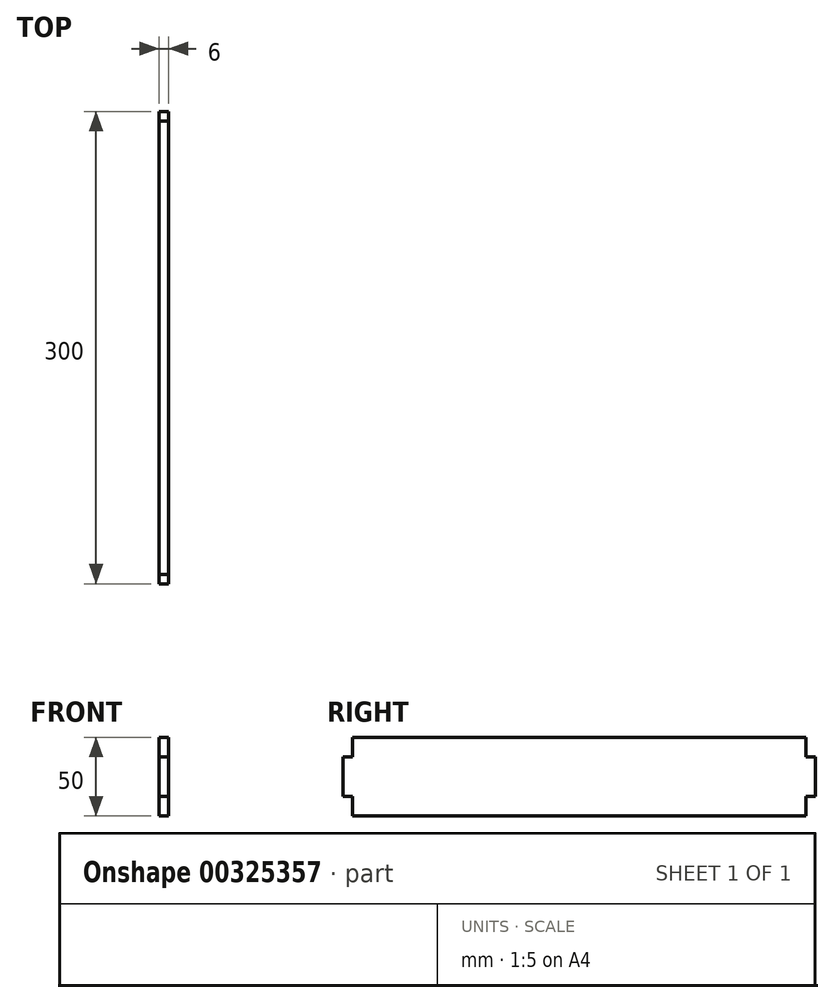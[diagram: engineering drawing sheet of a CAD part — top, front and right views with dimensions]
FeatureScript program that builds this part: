
annotation { "Feature Type Name" : "Feature", "Feature Type Description" : "" }
export const myFeature = defineFeature(function(context is Context, id is Id, definition is map)
    precondition{}
    {
        {
            var Q0;
            Q0=qCreatedBy(makeId("Right.planeOp"),FACE);
            var sketch = newSketch(context, id + "F0", { "sketchPlane" : qUnion([Q0])});
            skLineSegment(sketch, "E0.bottom", {"start": v(-144, 25) * mm, "end": v(144, 25) * mm});
            skLineSegment(sketch, "E0.top", {"start": v(-144, -25) * mm, "end": v(144, -25) * mm});
            skLineSegment(sketch, "E0.left", {"start": v(-144, 25) * mm, "end": v(-144, -25) * mm});
            skLineSegment(sketch, "E0.right", {"start": v(144, 25) * mm, "end": v(144, -25) * mm});
            skPoint(sketch, "E0.middle", {"position": v(0, 0) * mm});
            skLineSegment(sketch, "E1.bottom", {"start": v(-75, 25) * mm, "end": v(75, 25) * mm});
            skLineSegment(sketch, "E1.top", {"start": v(-75, 19) * mm, "end": v(75, 19) * mm});
            skLineSegment(sketch, "E1.left", {"start": v(-75, 25) * mm, "end": v(-75, 19) * mm});
            skLineSegment(sketch, "E1.right", {"start": v(75, 25) * mm, "end": v(75, 19) * mm});
            skPoint(sketch, "E1.middle", {"position": v(0, 22) * mm});
            skLineSegment(sketch, "E2.bottom", {"start": v(-144, 12.5) * mm, "end": v(-138, 12.5) * mm});
            skLineSegment(sketch, "E2.top", {"start": v(-144, -12.5) * mm, "end": v(-138, -12.5) * mm});
            skLineSegment(sketch, "E2.left", {"start": v(-144, 12.5) * mm, "end": v(-144, -12.5) * mm});
            skLineSegment(sketch, "E2.right", {"start": v(-138, 12.5) * mm, "end": v(-138, -12.5) * mm});
            skPoint(sketch, "E2.middle", {"position": v(-141, 0) * mm});
            skLineSegment(sketch, "E3.bottom", {"start": v(144, 12.5) * mm, "end": v(138, 12.5) * mm});
            skLineSegment(sketch, "E3.top", {"start": v(144, -12.5) * mm, "end": v(138, -12.5) * mm});
            skLineSegment(sketch, "E3.left", {"start": v(144, 12.5) * mm, "end": v(144, -12.5) * mm});
            skLineSegment(sketch, "E3.right", {"start": v(138, 12.5) * mm, "end": v(138, -12.5) * mm});
            skPoint(sketch, "E3.middle", {"position": v(141, 0) * mm});
            skPoint(sketch, "E3.middle.positionSnap0", {"position": v(144, 0) * mm});
            skPoint(sketch, "E3.centerSnap0", {"position": v(144, 0) * mm});
            skLineSegment(sketch, "E4.bottom", {"start": v(-75, -25) * mm, "end": v(75, -25) * mm});
            skLineSegment(sketch, "E4.top", {"start": v(-75, -19) * mm, "end": v(75, -19) * mm});
            skLineSegment(sketch, "E4.left", {"start": v(-75, -25) * mm, "end": v(-75, -19) * mm});
            skLineSegment(sketch, "E4.right", {"start": v(75, -25) * mm, "end": v(75, -19) * mm});
            skPoint(sketch, "E4.middle", {"position": v(0, -22) * mm});
            skLineSegment(sketch, "E5.top", {"start": v(-75, 31) * mm, "end": v(75, 31) * mm});
            skLineSegment(sketch, "E5.left", {"start": v(-75, 25) * mm, "end": v(-75, 31) * mm});
            skLineSegment(sketch, "E5.right", {"start": v(75, 25) * mm, "end": v(75, 31) * mm});
            skLineSegment(sketch, "E6.top", {"start": v(-75, -31) * mm, "end": v(75, -31) * mm});
            skLineSegment(sketch, "E6.left", {"start": v(-75, -25) * mm, "end": v(-75, -31) * mm});
            skLineSegment(sketch, "E6.right", {"start": v(75, -25) * mm, "end": v(75, -31) * mm});
            skLineSegment(sketch, "E7.bottom", {"start": v(-144, 12.5) * mm, "end": v(-150, 12.5) * mm});
            skLineSegment(sketch, "E7.top", {"start": v(-144, -12.5) * mm, "end": v(-150, -12.5) * mm});
            skLineSegment(sketch, "E7.right", {"start": v(-150, 12.5) * mm, "end": v(-150, -12.5) * mm});
            skLineSegment(sketch, "E8.bottom", {"start": v(144, 12.5) * mm, "end": v(150, 12.5) * mm});
            skLineSegment(sketch, "E8.top", {"start": v(144, -12.5) * mm, "end": v(150, -12.5) * mm});
            skLineSegment(sketch, "E8.right", {"start": v(150, 12.5) * mm, "end": v(150, -12.5) * mm});
            skSolve(sketch);
        }
        {
            var Q0;
            Q0=makeQuery(id+"F0.imprint","IMPRINT",FACE,{"disambiguationData":[TD([[makeQuery(id+"F0.imprint","IMPRINT",EDGE,{"derivedFrom":sQuery(id+"F0.wireOp",EDGE,"E1.top")}),-1.0]])]});
            var Q1;
            Q1=makeQuery(id+"F0.imprint","IMPRINT",FACE,{"disambiguationData":[TD([[makeQuery(id+"F0.imprint","IMPRINT",EDGE,{"derivedFrom":sQuery(id+"F0.wireOp",EDGE,"E1.bottom")}),1.0]])]});
            var Q2;
            Q2=makeQuery(id+"F0.imprint","IMPRINT",FACE,{"disambiguationData":[TD([[makeQuery(id+"F0.imprint","IMPRINT",EDGE,{"derivedFrom":sQuery(id+"F0.wireOp",EDGE,"E1.top")}),1.0]])]});
            var Q3;
            Q3=makeQuery(id+"F0.imprint","IMPRINT",FACE,{"disambiguationData":[TD([[makeQuery(id+"F0.imprint","IMPRINT",EDGE,{"derivedFrom":sQuery(id+"F0.wireOp",EDGE,"E4.bottom")}),-1.0]])]});
            var Q4;
            Q4=makeQuery(id+"F0.imprint","IMPRINT",FACE,{"disambiguationData":[TD([[makeQuery(id+"F0.imprint","IMPRINT",EDGE,{"derivedFrom":sQuery(id+"F0.wireOp",EDGE,"E4.top")}),-1.0]])]});
            var Q5;
            Q5=makeQuery(id+"F0.imprint","IMPRINT",FACE,{"disambiguationData":[TD([[makeQuery(id+"F0.imprint","IMPRINT",EDGE,{"derivedFrom":sQuery(id+"F0.wireOp",EDGE,"E2.bottom")}),-1.0]])]});
            var Q6;
            Q6=makeQuery(id+"F0.imprint","IMPRINT",FACE,{"disambiguationData":[TD([[makeQuery(id+"F0.imprint","IMPRINT",EDGE,{"derivedFrom":sQuery(id+"F0.wireOp",EDGE,"E7.bottom")}),1.0]])]});
            var Q7;
            Q7=makeQuery(id+"F0.imprint","IMPRINT",FACE,{"disambiguationData":[TD([[makeQuery(id+"F0.imprint","IMPRINT",EDGE,{"derivedFrom":sQuery(id+"F0.wireOp",EDGE,"E8.bottom")}),-1.0]])]});
            var Q8;
            Q8=makeQuery(id+"F0.imprint","IMPRINT",FACE,{"disambiguationData":[TD([[makeQuery(id+"F0.imprint","IMPRINT",EDGE,{"derivedFrom":sQuery(id+"F0.wireOp",EDGE,"E3.bottom")}),1.0]])]});
            extrude(context, id + "F1", {"entities" : qUnion([Q0, Q1, Q2, Q3, Q4, Q5, Q6, Q7, Q8]), "depth" : 6 * mm});
        }
    });
